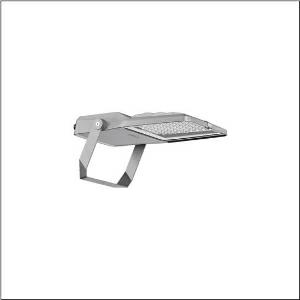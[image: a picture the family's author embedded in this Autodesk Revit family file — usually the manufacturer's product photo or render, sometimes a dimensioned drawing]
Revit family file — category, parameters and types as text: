
# Revit family: floodlight_fl_21_iq_mini___pl52_5xa7771c2d1a_0a7e
name_source: partatom
category: Lighting Fixtures
units: mm (PartAtom-declared; Revit-internal decimal feet)

## family parameters
Cut with Voids When Loaded = No
Host = Face
Light Source = No
Part Type = Normal
Room Calculation Point = No
Round Connector Dimension = Use Diameter
Shared = No

## types (1)
- --- (1 x LED, 12210 lm, 87.2 W, 3000K)
    Apparent Load = 87 VA
    CIE Flux Codes = 26 60 98 100 100
    Color Rendering = 70
    Color Temperature = 3000K
    Default Elevation = 1800 mm
    Description = Floodlight FL 21 iQ mini, floodlight, primary light control with lens, of PMMA, primary optical cover: protective disc, of toughened safety glass, transparent, light distribution: PL52, light emission: direct distribution, installation type: surface-mounted, lamps: LED, High Power LED, rated values: 12.210lm | 87,2W | 140lm/W (begin service life); end service life: 12.210lm | 92,1W; at 50% lumin. flux: 6.105lm | 40,1W | 152,2lm/W, colour temperature: 3000K, colour rendering: CRI > 70, light colour: 730, light setting 1 begin service life: 100% | 12.210lm | 87,2W | 140lm/W | 3.000K, light setting 1 end service life: 92,1W, further light settings possible, control: Auto-Match, Temp-Guard, Lumen-Switch, Night-Set, Smart-Wire, Light-Fading, Desk-Remote (wireless, voltage-free reading and setting of iQ features in the workshop via application-optimized NFC function/RFID function), optimised constant luminous flux control (CLO 2.0), pre-setting: linear dimming characteristic, with terminal, 6-pole, mains connection: 220..240V, AC, 50/60Hz, luminaire housing, of diecast aluminium, powder-coated, SITECO metallic grey (DB 702S), corrosivity category C5 mid according to DIN EN ISO 12944suitable for swimming poolschlorine-resistant, sealing non-destructively replaceable, mounting bracket, of steel, galvanised, powder-coated, SITECO metallic grey (DB 702S), protection rating (complete): IP66, insulation class (complete): insulation class II (safety insulation), certification: CE, ENEC, VDE, protection symbol: D, impact resistance: IK08, permissible operating ambient temperature: -40..+40°C, permissible operating ambient temperature for outdoor applications: -40..+50°C, standard: DIN EN 12944, LABS conformity tested according to VDMA 24364:2018-05, packaging unit: 1 piece

Light Distribution: PL52
    Height = 70 mm
    Lamp = 1 x LED
    Lamp Light Flux = 12210 lm
    Lamp Power = 87.2 W
    Lamp count = 1
    Length = 485 mm
    Luminous efficacy = 140 lm/W
    Manufacturer = Siteco
    ModVariant = No
    Model = 5XA7771C2D1A
    Number of Poles = 1
    OnlyDefault = Yes
    Power Factor = 1
    Product Name = Floodlight FL 21 iQ mini | PL52
    Product group = floodlight | pylon annexe
    ProductGroupID = 6201
    Protection Class = Protection class II
    Protection Degree = IP 66
    RLX_Detail_Level = 1
    RLX_Emergency_Light_Flux = 0 lm
    RLX_Emergency_Type = 0
    RLX_Emergency_Type_DB = No
    RlxData = <blob elided: 96801 chars, md5=dd0bc7f0>
    Socket = socket
    Standby Power = 0 W
    System Light Flux = 12210 lm
    System Power = 87 W
    Type Comments = factory setting: luminous flux: 100 % | dim-lin: 254 | 456 mA
    Type Image = l_1006845.jpg
    URL = http://relux.com
    VarID = @adj_164097
    Voltage = 0 V
    Weight = 0.00 kg
    Width = 337 mm

## geometry (parser evidence)
native form markers: Blend x4, Sweep x13
no freeform markers — native parametric forms only
